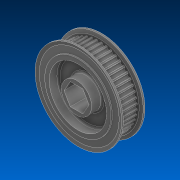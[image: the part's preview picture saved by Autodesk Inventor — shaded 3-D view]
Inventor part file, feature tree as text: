
AUTODESK INVENTOR PART (.ipt)
format: ipt  version: 2022.2 (Build 262287000, 287)  size: 557,056 bytes
history: native  units: in
note: dims shown in document units (in); Inventor stores cm internally (conversion verified against a paired STEP export)
features: fillet x1
ambient origin geometry x8: Origin, YZ Plane, XZ Plane, XY Plane, X Axis, Y Axis, Z Axis, Center Point
bodies: Solid1 (feature_tree)
feature tree (1):
  fillet  "Fillet1"  [1 undecoded]
note: 1 required parameter value undecoded (feature->parameter linkage not recoverable at this tier; creation-order binding heuristic only, values carry confidence <= 0.55)
